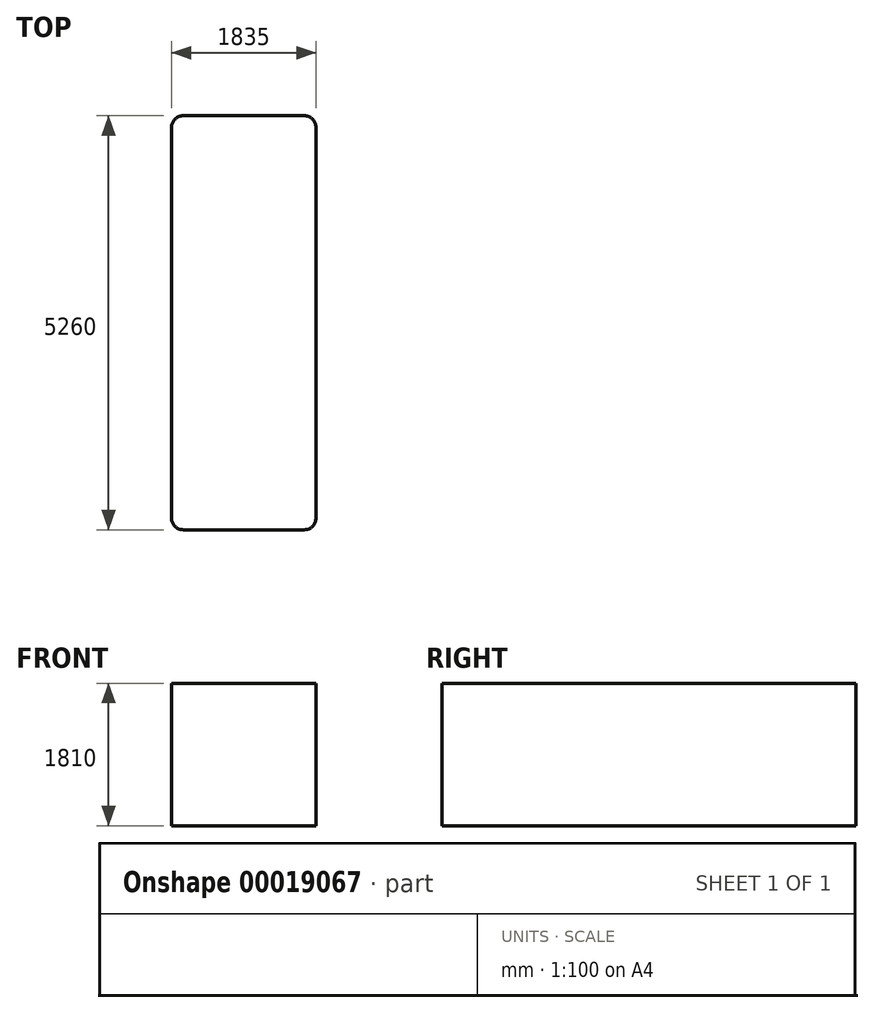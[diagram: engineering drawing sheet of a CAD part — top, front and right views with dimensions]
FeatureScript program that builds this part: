
annotation { "Feature Type Name" : "Feature", "Feature Type Description" : "" }
export const myFeature = defineFeature(function(context is Context, id is Id, definition is map)
    precondition{}
    {
        {
            var Q0;
            Q0=qCreatedBy(makeId("Top.planeOp"),FACE);
            var sketch = newSketch(context, id + "F0", { "sketchPlane" : qUnion([Q0])});
            skLineSegment(sketch, "E0.bottom", {"start": v(150, 0) * mm, "end": v(1685, 0) * mm});
            skLineSegment(sketch, "E0.top", {"start": v(150, 5260) * mm, "end": v(1685, 5260) * mm});
            skLineSegment(sketch, "E0.left", {"start": v(0, 150) * mm, "end": v(0, 5110) * mm});
            skLineSegment(sketch, "E0.right", {"start": v(1835, 150) * mm, "end": v(1835, 5110) * mm});
            skPoint(sketch, "E1.visualSharp", {"position": v(0, 5260) * mm});
            skArc(sketch, "E1.filletArc", {"start": v(150, 5260) * mm, "mid": v(43.93, 5216.07) * mm, "end": v(0, 5110) * mm});
            skPoint(sketch, "E2.visualSharp", {"position": v(1835, 5260) * mm});
            skArc(sketch, "E2.filletArc", {"start": v(1835, 5110) * mm, "mid": v(1791.07, 5216.07) * mm, "end": v(1685, 5260) * mm});
            skPoint(sketch, "E3.visualSharp", {"position": v(1835, 0) * mm});
            skArc(sketch, "E3.filletArc", {"start": v(1685, 0) * mm, "mid": v(1791.07, 43.93) * mm, "end": v(1835, 150) * mm});
            skPoint(sketch, "E4.visualSharp", {"position": v(0, 0) * mm});
            skArc(sketch, "E4.filletArc", {"start": v(0, 150) * mm, "mid": v(43.93, 43.93) * mm, "end": v(150, 0) * mm});
            skSolve(sketch);
        }
        {
            var Q0;
            Q0=makeQuery(id+"F0.imprint","IMPRINT",FACE,{"disambiguationData":[TD([[makeQuery(id+"F0.imprint","IMPRINT",EDGE,{"derivedFrom":sQuery(id+"F0.wireOp",EDGE,"E0.bottom")}),1.0]])]});
            extrude(context, id + "F1", {"entities" : qUnion([Q0]), "depth" : 1810 * mm});
        }
    });
